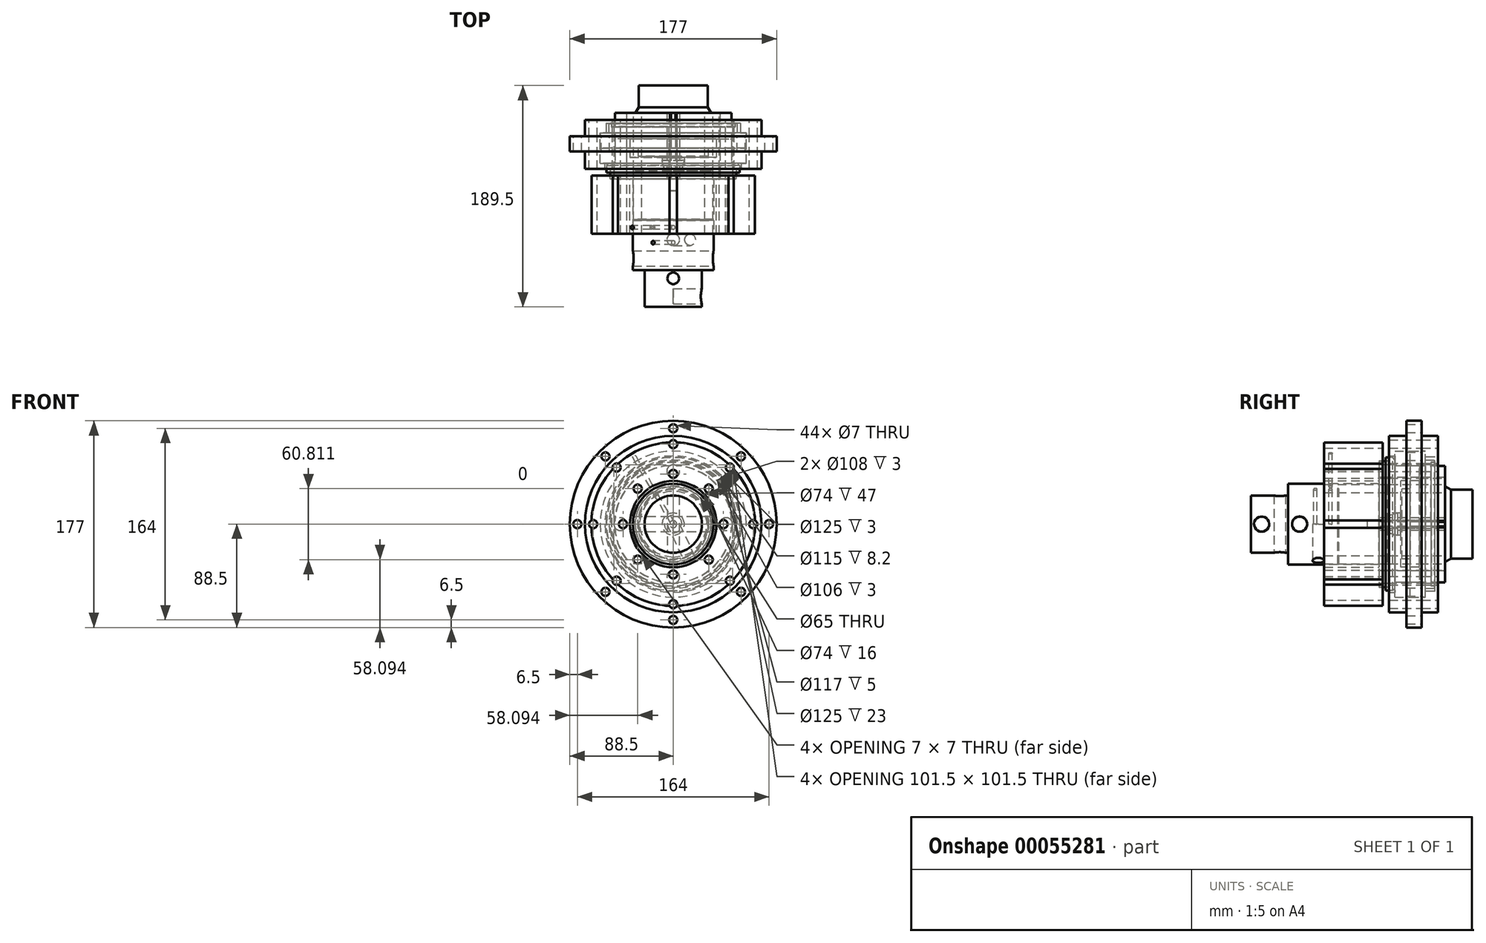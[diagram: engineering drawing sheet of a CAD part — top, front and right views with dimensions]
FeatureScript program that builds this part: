
annotation { "Feature Type Name" : "Feature", "Feature Type Description" : "" }
export const myFeature = defineFeature(function(context is Context, id is Id, definition is map)
    precondition{}
    {
        {
            var Q0;
            Q0=qCreatedBy(makeId("Top.planeOp"),FACE);
            var sketch = newSketch(context, id + "F0", { "sketchPlane" : qUnion([Q0])});
            skLineSegment(sketch, "E0", {"start": v(0, 23.5) * mm, "end": v(-29.5, 23.5) * mm});
            skLineSegment(sketch, "E1", {"start": v(-29.5, 23.5) * mm, "end": v(-29.5, 5) * mm});
            skLineSegment(sketch, "E2", {"start": v(-29.5, 5) * mm, "end": v(-32.39, 0) * mm});
            skLineSegment(sketch, "E3", {"start": v(-32.39, 0) * mm, "end": v(-50, 0) * mm});
            skLineSegment(sketch, "E4", {"start": v(-50, 0) * mm, "end": v(-50, -12) * mm});
            skLineSegment(sketch, "E5", {"start": v(-50, -12) * mm, "end": v(-37, -12) * mm});
            skLineSegment(sketch, "E6", {"start": v(-37, -12) * mm, "end": v(-37, -30) * mm});
            skLineSegment(sketch, "E7", {"start": v(-37, -30) * mm, "end": v(-30, -30) * mm});
            skLineSegment(sketch, "E8", {"start": v(-30, -30) * mm, "end": v(-30, -37) * mm});
            skLineSegment(sketch, "E9", {"start": v(-30, -37) * mm, "end": v(0, -37) * mm});
            skLineSegment(sketch, "E10", {"start": v(0, -37) * mm, "end": v(0, 23.5) * mm});
            skSolve(sketch);
        }
        {
            var Q0;
            Q0=makeQuery(id+"F0.imprint","IMPRINT",FACE,{"disambiguationData":[TD([[makeQuery(id+"F0.imprint","IMPRINT",EDGE,{"derivedFrom":sQuery(id+"F0.wireOp",EDGE,"E0")}),1.0]])]});
            var Q1;
            Q1=sQuery(id+"F0.wireOp",EDGE,"E10");
            revolve(context, id + "F1", {"entities" : qUnion([Q0]), "axis" : qUnion([Q1]), "revolveType" : RevolveType.FULL});
        }
        {
            var Q0;
            Q0=makeQuery(id+"F1.opRevolve","SWEPT_FACE",FACE,{"disambiguationData":[OSD([sQuery(id+"F0.wireOp",EDGE,"E5")])]});
            var sketch = newSketch(context, id + "F2", { "sketchPlane" : qUnion([Q0])});
            skCircle(sketch, "E11", {"center": v(0, 0) * mm, "radius": 37 * mm});
            skCircle(sketch, "E12", {"center": v(0, 0) * mm, "radius": 55 * mm});
            skLineSegment(sketch, "E13", {"start": v(-50, 0) * mm, "end": v(-55, 0) * mm});
            skSolve(sketch);
        }
        {
            var Q0;
            Q0 = qSketchRegion(id + "F2", true);
            extrude(context, id + "F3", {"entities" : qUnion([Q0]), "depth" : 5 * mm});
        }
        {
            var Q0;
            Q0=makeQuery(id+"F3.opExtrude","CAP_FACE",FACE,{"disambiguationData":[OSD([sQuery(id+"F2.wireOp",EDGE,"E11"),sQuery(id+"F2.wireOp",EDGE,"E12")])],"isStart":true});
            var sketch = newSketch(context, id + "F4", { "sketchPlane" : qUnion([Q0])});
            skCircle(sketch, "E14", {"center": v(0, 0) * mm, "radius": 55 * mm});
            skCircle(sketch, "E15", {"center": v(0, 0) * mm, "radius": 53 * mm});
            skLineSegment(sketch, "E16", {"start": v(55, 0) * mm, "end": v(53, 0) * mm});
            skSolve(sketch);
        }
        {
            var Q0;
            Q0=makeQuery(id+"F4.imprint","IMPRINT",FACE,{"disambiguationData":[TD([[makeQuery(id+"F4.imprint","IMPRINT",EDGE,{"derivedFrom":sQuery(id+"F4.wireOp",EDGE,"E14")}),-1.0]])]});
            extrude(context, id + "F5", {"entities" : qUnion([Q0]), "operationType" : NewBodyOperationType.ADD, "depth" : 3 * mm});
        }
        {
            var Q0;
            Q0=makeQuery(id+"F3.opExtrude","CAP_FACE",FACE,{"disambiguationData":[OSD([sQuery(id+"F2.wireOp",EDGE,"E11"),sQuery(id+"F2.wireOp",EDGE,"E12")])],"isStart":false});
            var sketch = newSketch(context, id + "F6", { "sketchPlane" : qUnion([Q0])});
            skCircle(sketch, "E17", {"center": v(0, 0) * mm, "radius": 37 * mm});
            skCircle(sketch, "E18", {"center": v(0, 0) * mm, "radius": 50 * mm});
            skSolve(sketch);
        }
        {
            var Q0;
            Q0 = qSketchRegion(id + "F6", true);
            extrude(context, id + "F7", {"entities" : qUnion([Q0]), "operationType" : NewBodyOperationType.ADD, "depth" : 5 * mm});
        }
        {
            var Q0;
            Q0=makeQuery(id+"F3.opExtrude","CAP_FACE",FACE,{"disambiguationData":[OSD([sQuery(id+"F2.wireOp",EDGE,"E11"),sQuery(id+"F2.wireOp",EDGE,"E12")])],"isStart":false});
            var sketch = newSketch(context, id + "F8", { "sketchPlane" : qUnion([Q0])});
            skCircle(sketch, "E19", {"center": v(0, 0) * mm, "radius": 50 * mm});
            skCircle(sketch, "E20", {"center": v(0, 0) * mm, "radius": 62.5 * mm});
            skSolve(sketch);
        }
        {
            var Q0;
            Q0 = qSketchRegion(id + "F8", true);
            extrude(context, id + "F9", {"entities" : qUnion([Q0]), "depth" : 13 * mm});
        }
        {
            var Q0;
            Q0=makeQuery(id+"F9.opExtrude","SWEPT_BODY",BODY,{"disambiguationData":[OSD([sQuery(id+"F8.wireOp",EDGE,"E19"),sQuery(id+"F8.wireOp",EDGE,"E20")])]});
            transform(context, id + "F10", {"entities" : qUnion([Q0]), "transformType" : TransformType.TRANSLATION_3D, "dx" : 0 * mm, "dy" : -13 * mm, "dz" : 0 * mm, "makeCopy" : true});
        }
        {
            var Q0;
            Q0=qCreatedBy(makeId("Top.planeOp"),FACE);
            var sketch = newSketch(context, id + "F11", { "sketchPlane" : qUnion([Q0])});
            skLineSegment(sketch, "E21", {"start": v(-57.5, -17) * mm, "end": v(-62.5, -17) * mm});
            skLineSegment(sketch, "E22", {"start": v(-75.5, -17) * mm, "end": v(-75.5, -6) * mm});
            skLineSegment(sketch, "E23", {"start": v(-75.5, -6) * mm, "end": v(-50.2, -6) * mm});
            skLineSegment(sketch, "E24", {"start": v(-50.2, -6) * mm, "end": v(-50.2, -11.8) * mm});
            skLineSegment(sketch, "E25", {"start": v(-50.2, -11.8) * mm, "end": v(-52.8, -11.8) * mm});
            skLineSegment(sketch, "E26", {"start": v(-52.8, -11.8) * mm, "end": v(-52.8, -8.8) * mm});
            skLineSegment(sketch, "E27", {"start": v(-52.8, -8.8) * mm, "end": v(-57.5, -8.8) * mm});
            skLineSegment(sketch, "E28", {"start": v(-57.5, -8.8) * mm, "end": v(-57.5, -17) * mm});
            skLineSegment(sketch, "E29", {"start": v(0, -19.93) * mm, "end": v(0, 5.88) * mm, "construction": true});
            skLineSegment(sketch, "E30", {"start": v(-75.5, -17) * mm, "end": v(-75.5, -20) * mm});
            skLineSegment(sketch, "E31", {"start": v(-75.5, -20) * mm, "end": v(-62.5, -20) * mm});
            skLineSegment(sketch, "E32", {"start": v(-62.5, -20) * mm, "end": v(-62.5, -17) * mm});
            skSolve(sketch);
        }
        {
            var Q0;
            Q0 = qSketchRegion(id + "F11", true);
            var Q1;
            Q1=sQuery(id+"F11.wireOp",EDGE,"E29");
            revolve(context, id + "F12", {"entities" : qUnion([Q0]), "axis" : qUnion([Q1]), "revolveType" : RevolveType.FULL});
        }
        {
            var Q0;
            Q0=qCreatedBy(makeId("Top.planeOp"),FACE);
            var sketch = newSketch(context, id + "F13", { "sketchPlane" : qUnion([Q0])});
            skLineSegment(sketch, "E33", {"start": v(-9.5, -38) * mm, "end": v(-37, -38) * mm});
            skLineSegment(sketch, "E34", {"start": v(-37, -38) * mm, "end": v(-37, -22) * mm});
            skLineSegment(sketch, "E35", {"start": v(-37, -22) * mm, "end": v(-50, -22) * mm});
            skLineSegment(sketch, "E36", {"start": v(-50, -22) * mm, "end": v(-50, -43) * mm});
            skLineSegment(sketch, "E37", {"start": v(-50, -43) * mm, "end": v(-55, -43) * mm});
            skLineSegment(sketch, "E38", {"start": v(-57, -45) * mm, "end": v(-57, -51) * mm});
            skLineSegment(sketch, "E39", {"start": v(-57, -51) * mm, "end": v(-54, -51) * mm});
            skLineSegment(sketch, "E40", {"start": v(-54, -51) * mm, "end": v(-54, -48) * mm});
            skLineSegment(sketch, "E41", {"start": v(-54, -48) * mm, "end": v(-9.5, -48) * mm});
            skLineSegment(sketch, "E42", {"start": v(0, -48) * mm, "end": v(0, -38) * mm, "construction": true});
            skLineSegment(sketch, "E43", {"start": v(-55, -43) * mm, "end": v(-57, -45) * mm});
            skLineSegment(sketch, "E44", {"start": v(-9.5, -48) * mm, "end": v(-9.5, -38) * mm});
            skSolve(sketch);
        }
        {
            var Q0;
            Q0 = qSketchRegion(id + "F13", true);
            var Q1;
            Q1=sQuery(id+"F13.wireOp",EDGE,"E42");
            revolve(context, id + "F14", {"entities" : qUnion([Q0]), "axis" : qUnion([Q1]), "revolveType" : RevolveType.FULL});
        }
        {
            var Q0;
            Q0=qCreatedBy(makeId("Top.planeOp"),FACE);
            var sketch = newSketch(context, id + "F15", { "sketchPlane" : qUnion([Q0])});
            skLineSegment(sketch, "E45.bottom", {"start": v(-3, -56.5) * mm, "end": v(-54, -56.5) * mm});
            skLineSegment(sketch, "E45.top", {"start": v(-32.5, -48) * mm, "end": v(-54, -48) * mm});
            skLineSegment(sketch, "E45.left", {"start": v(0, -56.5) * mm, "end": v(0, -48) * mm, "construction": true});
            skLineSegment(sketch, "E45.right", {"start": v(-54, -56.5) * mm, "end": v(-54, -48) * mm});
            skLineSegment(sketch, "E46", {"start": v(-3, -56.5) * mm, "end": v(-3, -38.3) * mm});
            skLineSegment(sketch, "E47", {"start": v(-3, -38.3) * mm, "end": v(-9.5, -38.3) * mm});
            skLineSegment(sketch, "E48", {"start": v(-9.5, -38.3) * mm, "end": v(-9.5, -40.54) * mm});
            skLineSegment(sketch, "E49", {"start": v(-9.5, -40.54) * mm, "end": v(-7.5, -48) * mm});
            skLineSegment(sketch, "E50.top", {"start": v(-32.5, -51) * mm, "end": v(-7.5, -51) * mm});
            skLineSegment(sketch, "E50.left", {"start": v(-32.5, -48) * mm, "end": v(-32.5, -51) * mm});
            skLineSegment(sketch, "E50.right", {"start": v(-7.5, -48) * mm, "end": v(-7.5, -51) * mm});
            skEllipse(sketch, "E51", {"center": v(-30.5, -49.5) * mm, "majorRadius": 2 * mm, "minorRadius": 1.5 * mm, "majorAxis": v(-1, 0)});
            skSolve(sketch);
        }
        {
            var Q0;
            Q0 = qSketchRegion(id + "F15", true);
            var Q1;
            Q1=sQuery(id+"F15.wireOp",EDGE,"E45.left");
            revolve(context, id + "F16", {"entities" : qUnion([Q0]), "axis" : qUnion([Q1]), "revolveType" : RevolveType.FULL});
        }
        {
            var Q0;
            Q0=qCreatedBy(makeId("Top.planeOp"),FACE);
            var sketch = newSketch(context, id + "F17", { "sketchPlane" : qUnion([Q0])});
            skLineSegment(sketch, "E52", {"start": v(0, -66.5) * mm, "end": v(-3, -66.5) * mm});
            skLineSegment(sketch, "E53", {"start": v(-3, -66.5) * mm, "end": v(-3, -56.5) * mm});
            skLineSegment(sketch, "E54", {"start": v(-3, -56.5) * mm, "end": v(-34.5, -56.5) * mm});
            skLineSegment(sketch, "E55", {"start": v(-34.5, -56.5) * mm, "end": v(-34.5, -91) * mm});
            skLineSegment(sketch, "E56", {"start": v(-34.5, -134.5) * mm, "end": v(-24.5, -134.5) * mm});
            skLineSegment(sketch, "E57", {"start": v(0, -134.5) * mm, "end": v(0, -66.5) * mm});
            skLineSegment(sketch, "E58", {"start": v(0, -134.5) * mm, "end": v(0, -166) * mm});
            skLineSegment(sketch, "E59", {"start": v(0, -166) * mm, "end": v(-24.5, -166) * mm});
            skLineSegment(sketch, "E60", {"start": v(-24.5, -166) * mm, "end": v(-24.5, -134.5) * mm});
            skLineSegment(sketch, "E61", {"start": v(-34, -91.5) * mm, "end": v(0, -91.5) * mm});
            skLineSegment(sketch, "E62", {"start": v(-34.5, -91) * mm, "end": v(-34, -91.5) * mm});
            skLineSegment(sketch, "E63", {"start": v(-34, -91.5) * mm, "end": v(-34.5, -92) * mm});
            skLineSegment(sketch, "E64.trimOffspring", {"start": v(-34.5, -92) * mm, "end": v(-34.5, -134.5) * mm});
            skSolve(sketch);
        }
        {
            var Q0;
            Q0 = qSketchRegion(id + "F17", true);
            var Q1;
            Q1=sQuery(id+"F17.wireOp",EDGE,"E57");
            revolve(context, id + "F18", {"entities" : qUnion([Q0]), "axis" : qUnion([Q1]), "revolveType" : RevolveType.FULL});
        }
        {
            var Q0;
            Q0=qCreatedBy(makeId("Top.planeOp"),FACE);
            var sketch = newSketch(context, id + "F19", { "sketchPlane" : qUnion([Q0])});
            skLineSegment(sketch, "E65", {"start": v(-37, -56.5) * mm, "end": v(-54, -56.5) * mm});
            skLineSegment(sketch, "E66", {"start": v(-54, -56.5) * mm, "end": v(-54, -53.5) * mm});
            skLineSegment(sketch, "E67", {"start": v(-54, -53.5) * mm, "end": v(-70, -53.5) * mm});
            skLineSegment(sketch, "E68", {"start": v(-70, -53.5) * mm, "end": v(-70, -103.5) * mm});
            skLineSegment(sketch, "E69", {"start": v(-70, -103.5) * mm, "end": v(-37, -103.5) * mm});
            skLineSegment(sketch, "E70", {"start": v(-37, -103.5) * mm, "end": v(-37, -56.5) * mm});
            skLineSegment(sketch, "E71", {"start": v(0, -56.5) * mm, "end": v(0, -103.5) * mm});
            skSolve(sketch);
        }
        {
            var Q0;
            Q0 = qSketchRegion(id + "F19", true);
            var Q1;
            Q1=sQuery(id+"F19.wireOp",EDGE,"E71");
            revolve(context, id + "F20", {"entities" : qUnion([Q0]), "axis" : qUnion([Q1]), "revolveType" : RevolveType.FULL});
        }
        {
            var Q0;
            Q0=qCreatedBy(makeId("Top.planeOp"),FACE);
            var sketch = newSketch(context, id + "F21", { "sketchPlane" : qUnion([Q0])});
            skLineSegment(sketch, "E72", {"start": v(-58.5, -43) * mm, "end": v(-58.5, -48) * mm});
            skLineSegment(sketch, "E73", {"start": v(-58.5, -48) * mm, "end": v(-75.5, -48) * mm});
            skLineSegment(sketch, "E74", {"start": v(-75.5, -48) * mm, "end": v(-75.5, -20) * mm});
            skLineSegment(sketch, "E75", {"start": v(-75.5, -20) * mm, "end": v(-62.5, -20) * mm});
            skLineSegment(sketch, "E76", {"start": v(-62.5, -20) * mm, "end": v(-62.5, -43) * mm});
            skLineSegment(sketch, "E77", {"start": v(-62.5, -43) * mm, "end": v(-58.5, -43) * mm});
            skLineSegment(sketch, "E78.bottom", {"start": v(-75.5, -20) * mm, "end": v(-88.5, -20) * mm});
            skLineSegment(sketch, "E78.top", {"start": v(-75.5, -33) * mm, "end": v(-88.5, -33) * mm});
            skLineSegment(sketch, "E78.left", {"start": v(-75.5, -20) * mm, "end": v(-75.5, -33) * mm});
            skLineSegment(sketch, "E78.right", {"start": v(-88.5, -20) * mm, "end": v(-88.5, -33) * mm});
            skLineSegment(sketch, "E79", {"start": v(0, -16.66) * mm, "end": v(0, -40.23) * mm, "construction": true});
            skSolve(sketch);
        }
        {
            var Q0;
            Q0 = qSketchRegion(id + "F21", true);
            var Q1;
            Q1=sQuery(id+"F21.wireOp",EDGE,"E79");
            revolve(context, id + "F22", {"entities" : qUnion([Q0]), "axis" : qUnion([Q1]), "revolveType" : RevolveType.FULL});
        }
        {
            var Q0;
            Q0=makeQuery(id+"F1.opRevolve","SWEPT_FACE",FACE,{"disambiguationData":[OSD([sQuery(id+"F0.wireOp",EDGE,"E3")])]});
            var sketch = newSketch(context, id + "F23", { "sketchPlane" : qUnion([Q0])});
            skCircle(sketch, "E80", {"center": v(-43, 0) * mm, "radius": 3.5 * mm});
            skCircle(sketch, "E81.1.0", {"center": v(-30.4, -30.4) * mm, "radius": 3.5 * mm});
            skCircle(sketch, "E81.2.0", {"center": v(0, -43) * mm, "radius": 3.5 * mm});
            skCircle(sketch, "E81.3.0", {"center": v(30.4, -30.4) * mm, "radius": 3.5 * mm});
            skCircle(sketch, "E81.4.0", {"center": v(43, 0) * mm, "radius": 3.5 * mm});
            skCircle(sketch, "E81.5.0", {"center": v(30.4, 30.4) * mm, "radius": 3.5 * mm});
            skCircle(sketch, "E81.6.0", {"center": v(0, 43) * mm, "radius": 3.5 * mm});
            skCircle(sketch, "E81.7.0", {"center": v(-30.4, 30.4) * mm, "radius": 3.5 * mm});
            skPoint(sketch, "E81.center", {"position": v(0, 0) * mm});
            skSolve(sketch);
        }
        {
            var Q0;
            Q0 = qSketchRegion(id + "F23", true);
            extrude(context, id + "F24", {"entities" : qUnion([Q0]), "operationType" : NewBodyOperationType.REMOVE, "endBound" : BoundingType.THROUGH_ALL, "oppositeDirection" : true, "depth" : 25 * mm});
        }
        {
            var Q0;
            Q0=makeQuery(id+"F12.opRevolve","SWEPT_FACE",FACE,{"disambiguationData":[OSD([sQuery(id+"F11.wireOp",EDGE,"E23")])]});
            var sketch = newSketch(context, id + "F25", { "sketchPlane" : qUnion([Q0])});
            skCircle(sketch, "E82", {"center": v(0, 68.5) * mm, "radius": 3.5 * mm});
            skCircle(sketch, "E83.1.0", {"center": v(-48.44, 48.44) * mm, "radius": 3.5 * mm});
            skCircle(sketch, "E83.2.0", {"center": v(-68.5, 0) * mm, "radius": 3.5 * mm});
            skPoint(sketch, "E83.center", {"position": v(0, 0) * mm});
            skCircle(sketch, "E84.1.3.0", {"center": v(-48.44, -48.44) * mm, "radius": 3.5 * mm});
            skCircle(sketch, "E84.1.4.0", {"center": v(0, -68.5) * mm, "radius": 3.5 * mm});
            skCircle(sketch, "E84.1.5.0", {"center": v(48.44, -48.44) * mm, "radius": 3.5 * mm});
            skCircle(sketch, "E84.1.6.0", {"center": v(68.5, 0) * mm, "radius": 3.5 * mm});
            skCircle(sketch, "E84.1.7.0", {"center": v(48.44, 48.44) * mm, "radius": 3.5 * mm});
            skSolve(sketch);
        }
        {
            var Q0;
            Q0 = qSketchRegion(id + "F25", true);
            extrude(context, id + "F26", {"entities" : qUnion([Q0]), "operationType" : NewBodyOperationType.REMOVE, "endBound" : BoundingType.THROUGH_ALL, "oppositeDirection" : true, "depth" : 25 * mm});
        }
        {
            var Q0;
            Q0=makeQuery(id+"F22.opRevolve","SWEPT_FACE",FACE,{"disambiguationData":[OSD([sQuery(id+"F21.wireOp",EDGE,"E75"),sQuery(id+"F21.wireOp",EDGE,"E78.bottom")])]});
            var sketch = newSketch(context, id + "F27", { "sketchPlane" : qUnion([Q0])});
            skCircle(sketch, "E85", {"center": v(0, 82) * mm, "radius": 3.5 * mm});
            skCircle(sketch, "E86.1.0", {"center": v(-57.98, 57.98) * mm, "radius": 3.5 * mm});
            skCircle(sketch, "E86.2.0", {"center": v(-82, 0) * mm, "radius": 3.5 * mm});
            skCircle(sketch, "E86.3.0", {"center": v(-57.98, -57.98) * mm, "radius": 3.5 * mm});
            skCircle(sketch, "E86.4.0", {"center": v(0, -82) * mm, "radius": 3.5 * mm});
            skCircle(sketch, "E86.5.0", {"center": v(57.98, -57.98) * mm, "radius": 3.5 * mm});
            skCircle(sketch, "E86.6.0", {"center": v(82, 0) * mm, "radius": 3.5 * mm});
            skCircle(sketch, "E86.7.0", {"center": v(57.98, 57.98) * mm, "radius": 3.5 * mm});
            skPoint(sketch, "E86.center", {"position": v(0, 0) * mm});
            skSolve(sketch);
        }
        {
            var Q0;
            Q0 = qSketchRegion(id + "F27", true);
            extrude(context, id + "F28", {"entities" : qUnion([Q0]), "operationType" : NewBodyOperationType.REMOVE, "endBound" : BoundingType.THROUGH_ALL, "oppositeDirection" : true, "depth" : 25 * mm});
        }
        {
            var Q0;
            Q0=qCreatedBy(makeId("Front.planeOp"),FACE);
            var sketch = newSketch(context, id + "F29", { "sketchPlane" : qUnion([Q0])});
            skCircle(sketch, "E87", {"center": v(0, 0) * mm, "radius": 100 * mm, "construction": true});
            skLineSegment(sketch, "E88", {"start": v(100, 0) * mm, "end": v(-100, 0) * mm, "construction": true});
            skLineSegment(sketch, "E89", {"start": v(-100, -100) * mm, "end": v(100, -100) * mm, "construction": true});
            skLineSegment(sketch, "E90", {"start": v(132.9, -48.37) * mm, "end": v(-48.37, -132.9) * mm, "construction": true});
            skPoint(sketch, "E91", {"position": v(42.26, -90.63) * mm});
            skLineSegment(sketch, "E92", {"start": v(100, -100) * mm, "end": v(100, 100) * mm, "construction": true});
            skLineSegment(sketch, "E93", {"start": v(-136.6, 36.6) * mm, "end": v(36.6, 136.6) * mm, "construction": true});
            skPoint(sketch, "E94", {"position": v(-50, 86.6) * mm});
            skSolve(sketch);
        }
        {
            var Q0;
            Q0=sQuery(id+"F29.wireOp",EDGE,"E93");
            cPlane(context, id + "F30", {"entities" : qUnion([Q0]), "cplaneType" : CPlaneType.LINE_ANGLE, "offset" : 150 * mm, "angle" : 90 * degree, "width" : 150 * mm, "height" : 150 * mm});
        }
        {
            var Q0;
            Q0=sQuery(id+"F29.wireOp",EDGE,"E89");
            cPlane(context, id + "F31", {"entities" : qUnion([Q0]), "cplaneType" : CPlaneType.LINE_ANGLE, "offset" : 150 * mm, "angle" : 90 * degree, "width" : 150 * mm, "height" : 150 * mm});
        }
        {
            var Q0;
            Q0=sQuery(id+"F29.wireOp",EDGE,"E92");
            cPlane(context, id + "F32", {"entities" : qUnion([Q0]), "cplaneType" : CPlaneType.LINE_ANGLE, "offset" : 150 * mm, "angle" : 0 * degree, "width" : 150 * mm, "height" : 150 * mm});
        }
        {
            var Q0;
            Q0=sQuery(id+"F29.wireOp",EDGE,"E90");
            cPlane(context, id + "F33", {"entities" : qUnion([Q0]), "cplaneType" : CPlaneType.LINE_ANGLE, "offset" : 150 * mm, "angle" : 90 * degree, "width" : 150 * mm, "height" : 150 * mm});
        }
        {
            var Q0;
            Q0=qCreatedBy(id+"F31.planeOp",FACE);
            var sketch = newSketch(context, id + "F34", { "sketchPlane" : qUnion([Q0])});
            skCircle(sketch, "E95", {"center": v(0, -141.5) * mm, "radius": 5 * mm});
            skSolve(sketch);
        }
        {
            var Q0;
            Q0 = qSketchRegion(id + "F34", true);
            extrude(context, id + "F35", {"entities" : qUnion([Q0]), "operationType" : NewBodyOperationType.REMOVE, "endBound" : BoundingType.THROUGH_ALL, "depth" : 25 * mm});
        }
        {
            var Q0;
            Q0=qCreatedBy(id+"F33.planeOp",FACE);
            var sketch = newSketch(context, id + "F36", { "sketchPlane" : qUnion([Q0])});
            skCircle(sketch, "E96", {"center": v(0, -108.5) * mm, "radius": 5 * mm});
            skSolve(sketch);
        }
        {
            var Q0;
            Q0 = qSketchRegion(id + "F36", true);
            var Q1;
            Q1=qCreatedBy(makeId("Top.planeOp"),FACE);
            extrude(context, id + "F37", {"entities" : qUnion([Q0]), "operationType" : NewBodyOperationType.REMOVE, "endBound" : BoundingType.UP_TO_SURFACE, "endBoundEntityFace" : qUnion([Q1]), "depth" : 25 * mm});
        }
        {
            var Q0;
            Q0=qCreatedBy(id+"F32.planeOp",FACE);
            var sketch = newSketch(context, id + "F38", { "sketchPlane" : qUnion([Q0])});
            skCircle(sketch, "E97", {"center": v(-124.5, 0) * mm, "radius": 6.5 * mm});
            skCircle(sketch, "E98", {"center": v(-157, 0) * mm, "radius": 6.5 * mm});
            skSolve(sketch);
        }
        {
            var Q0;
            Q0=makeQuery(id+"F38.imprint","IMPRINT",FACE,{"disambiguationData":[TD([[makeQuery(id+"F38.imprint","IMPRINT",EDGE,{"derivedFrom":sQuery(id+"F38.wireOp",EDGE,"E97")}),1.0]])]});
            var Q1;
            Q1=sQuery(id+"F38.wireOp",EDGE,"E97");
            extrude(context, id + "F39", {"entities" : qUnion([Q0]), "operationType" : NewBodyOperationType.REMOVE, "surfaceEntities" : qUnion([Q1]), "endBound" : BoundingType.THROUGH_ALL, "oppositeDirection" : true, "depth" : 25 * mm});
        }
        {
            var Q0;
            Q0=makeQuery(id+"F38.imprint","IMPRINT",FACE,{"disambiguationData":[TD([[makeQuery(id+"F38.imprint","IMPRINT",EDGE,{"derivedFrom":sQuery(id+"F38.wireOp",EDGE,"E98")}),1.0]])]});
            var Q1;
            Q1=qCreatedBy(makeId("Right.planeOp"),FACE);
            extrude(context, id + "F40", {"entities" : qUnion([Q0]), "operationType" : NewBodyOperationType.REMOVE, "endBound" : BoundingType.UP_TO_SURFACE, "oppositeDirection" : true, "endBoundEntityFace" : qUnion([Q1]), "depth" : 25 * mm});
        }
        {
            var Q0;
            Q0=qCreatedBy(id+"F30.planeOp",FACE);
            var sketch = newSketch(context, id + "F41", { "sketchPlane" : qUnion([Q0])});
            skCircle(sketch, "E99", {"center": v(0, -98) * mm, "radius": 1.5 * mm});
            skCircle(sketch, "E100", {"center": v(0, -111) * mm, "radius": 1.5 * mm});
            skSolve(sketch);
        }
        {
            var Q0;
            Q0 = qSketchRegion(id + "F41", true);
            var Q1;
            Q1=qCreatedBy(makeId("Top.planeOp"),FACE);
            extrude(context, id + "F42", {"entities" : qUnion([Q0]), "operationType" : NewBodyOperationType.REMOVE, "endBound" : BoundingType.UP_TO_SURFACE, "oppositeDirection" : true, "endBoundEntityFace" : qUnion([Q1]), "depth" : 25 * mm});
        }
        {
            var Q0;
            Q0=makeQuery(id+"F16.opRevolve","SWEPT_FACE",FACE,{"disambiguationData":[OSD([sQuery(id+"F15.wireOp",EDGE,"E45.bottom")])]});
            var sketch = newSketch(context, id + "F43", { "sketchPlane" : qUnion([Q0])});
            skCircle(sketch, "E101", {"center": v(-45.25, 0) * mm, "radius": 5.5 * mm});
            skCircle(sketch, "E102.1.0", {"center": v(0, -45.25) * mm, "radius": 5.5 * mm});
            skCircle(sketch, "E102.2.0", {"center": v(45.25, 0) * mm, "radius": 5.5 * mm});
            skCircle(sketch, "E102.3.0", {"center": v(0, 45.25) * mm, "radius": 5.5 * mm});
            skPoint(sketch, "E102.center", {"position": v(0, 0) * mm});
            skSolve(sketch);
        }
        {
            var Q0;
            Q0 = qSketchRegion(id + "F43", true);
            extrude(context, id + "F44", {"entities" : qUnion([Q0]), "operationType" : NewBodyOperationType.REMOVE, "endBound" : BoundingType.THROUGH_ALL, "oppositeDirection" : true, "depth" : 25 * mm});
        }
    });
